# Revit family: IS_iLifeA_T4725_BIM_GB
name_source: partatom
category: Plumbing Fixtures
units: mm (PartAtom-declared; Revit-internal decimal feet)

## family parameters
Always vertical = No
Cut with Voids When Loaded = No
OmniClass Number = 23.45.05.21.11.11
OmniClass Title = Water Operated Water Closets
Part Type = Normal
Room Calculation Point = No
Round Connector Dimension = Use Diameter
Shared = No
Work Plane-Based = No

## types (3) — shared parameters
Accessories = https://www.idealstandard.co.uk
AreaMeasurement = Internal
AreaUnits = millimetres
AssetType = Fixed
BIMObjectName = IS_IdealStandard_WCcisterns_i.lifeA_T4725
BIMobject category = Toilet Cisterns
BIMobject category code = toilet-cisterns
BIMobject main category = Sanitary
BIMobject main category code = sanitary
Brand = Ideal Standard
Brand url = http://www.idealstandard.co.uk
Category = Sanitary
CisternCapacity = 0.00 m³
CisternMaterial = Ceramics
ConnectionType = Plumbing
CurrencyUnit = £
CurrentRevision = 1
Date of publishing = 07/10/2022
DurationUnit = Years
Edition number = 1
ElementType = fixed
ExpectedLife = 99
Features = Cistern, side inlet, trim mounted, pre-adjusted, 6/3 l,
FlushRate = 0.00 m³
Help = https://www.idealstandard.co.uk
IFC Classification = Sanitary Terminal
IfcExportAs = IfcSanitaryTerminalType
IfcExportType = WASHHANDBASIN
Installation instructions = https://www.idealstandard.co.uk
InstallationDate = n /a
InstallationInstructions = https://www.idealstandard.co.uk
LinearUnits = millimetres
MaintenanceInformation = https://www.idealstandard.co.uk
Manufacturer = Ideal Standard
Manufacturer name = Ideal Standard
ManufacturerURL = https://www.idealstandard.co.uk
Masterformat 2014 Code = 22 40 00
Masterformat 2014 Description = Plumbing Fixtures
Material = Ceramics
Material main = Ceramics
ModelReference = Cistern, side inlet, trim mounted, pre-adjusted, 6/3 l,
NBS Reference Code = 45-35-70/384
NBS Reference Description = WC Pans
Name = WCcisterns_i.lifeA_T4725_IdealStandard
NettWeight = 11.4
NominalDepth = 164 mm
NominalHeight = 394 mm
NominalWidth = 355 mm
OmniClass Code = 23-31 19 00
OmniClass Description = Toilets
Product Guid = 855fd105-3790-4373-8a1a-83ae6ad12b98
Product SKU = T4725
Product certification = https://www.idealstandard.co.uk
Product data url = https://bimobject.com
Product family = i.life A
Product group = WC Cistern
Product name = IDEAL STANDARD I.LIFE A CISTERN, SIDE INLET, TRIM MOUNTED, PRE-ADJUSTED, 6/3 L
Product url = https://www.idealstandard.co.uk
ProductInformation = https://www.idealstandard.co.uk
QR code = http://bimobject.com
Shape = sculptured
Size = 355 x 164 x 394 mm
Space = Internal
SpareParts = https://www.idealstandard.co.uk
Technical description = https://www.idealstandard.co.uk
UNSPSC Code = 301815
URL = https://www.idealstandard.co.uk
Uniclass 1.4 Code = L72164
Uniclass 1.4 Description = WC Cisterns
Uniclass 2.0 Code = Pr_40_35_93_90
Uniclass 2.0 Description = Wc Cisterns
Uniclass 2015 Code = Pr_40_20_93_89
Uniclass 2015 Name = WC cisterns
Uniclass2015Code = Pr_40_20_93_89
Uniclass2015Title = WC cisterns
Uniclass2015Version = v1.27
Uniformat II Code = D2010
Uniformat II Description = Plumbing Fixtures
Version = 1
VolumeUnits = liters
WRASURL = https://www.wrasapprovals.co.uk
WarrantyDescription = manufacturer warranty
WarrantyDurationUnit = years
Weight Net (Kg) = 11.4
Youtube clip = https://www.youtube.com
zero-valued in all types: Cost, Default Elevation, FlushingRate

## per-type parameters (varying)
| type | BarCode | CisternColor | Color | Description | Finish | GTIN code | MainColor | Model | ModelNumber |
| T472501 - Ideal Standard i.life A cistern, side inlet, trim mounted, pre-adjusted, 6/3 l, white | 8014140487012 | White | White | Ideal Standard i.life A cistern, side inlet, trim mounted, pre-adjusted, 6/3 l, white | White | 8014140487012 | White | T472501 | T472501 |
| T4725HY - Ideal Standard i.life A cistern, side inlet, trim mounted, pre-adjusted, 6/3 l - Antibacterial glaze Smartguard+ | 8014140514732 | White | White | Ideal Standard i.life A cistern, side inlet, trim mounted, pre-adjusted, 6/3 l, antibacterial glaze Smartguard+, in carton box, EU pallet | White | 8014140514732 | White | T4725HY | T4725HY |
| T472558 - Ideal Standard i.life A cistern, side inlet, trim mounted, pre-adjusted, 6/3 l - Glossy grey | 8014140511793 | Glossy grey | Glossy grey | Ideal Standard i.life A cistern, side inlet, trim mounted, pre-adjusted, 6/3 l, glossy grey, in carton box, EU pallet | Glossy grey | 8014140511793 | Glossy grey | T472558 | T472558 |

## geometry (parser evidence)
native form markers: Blend x4, Sweep x3
no freeform markers — native parametric forms only
